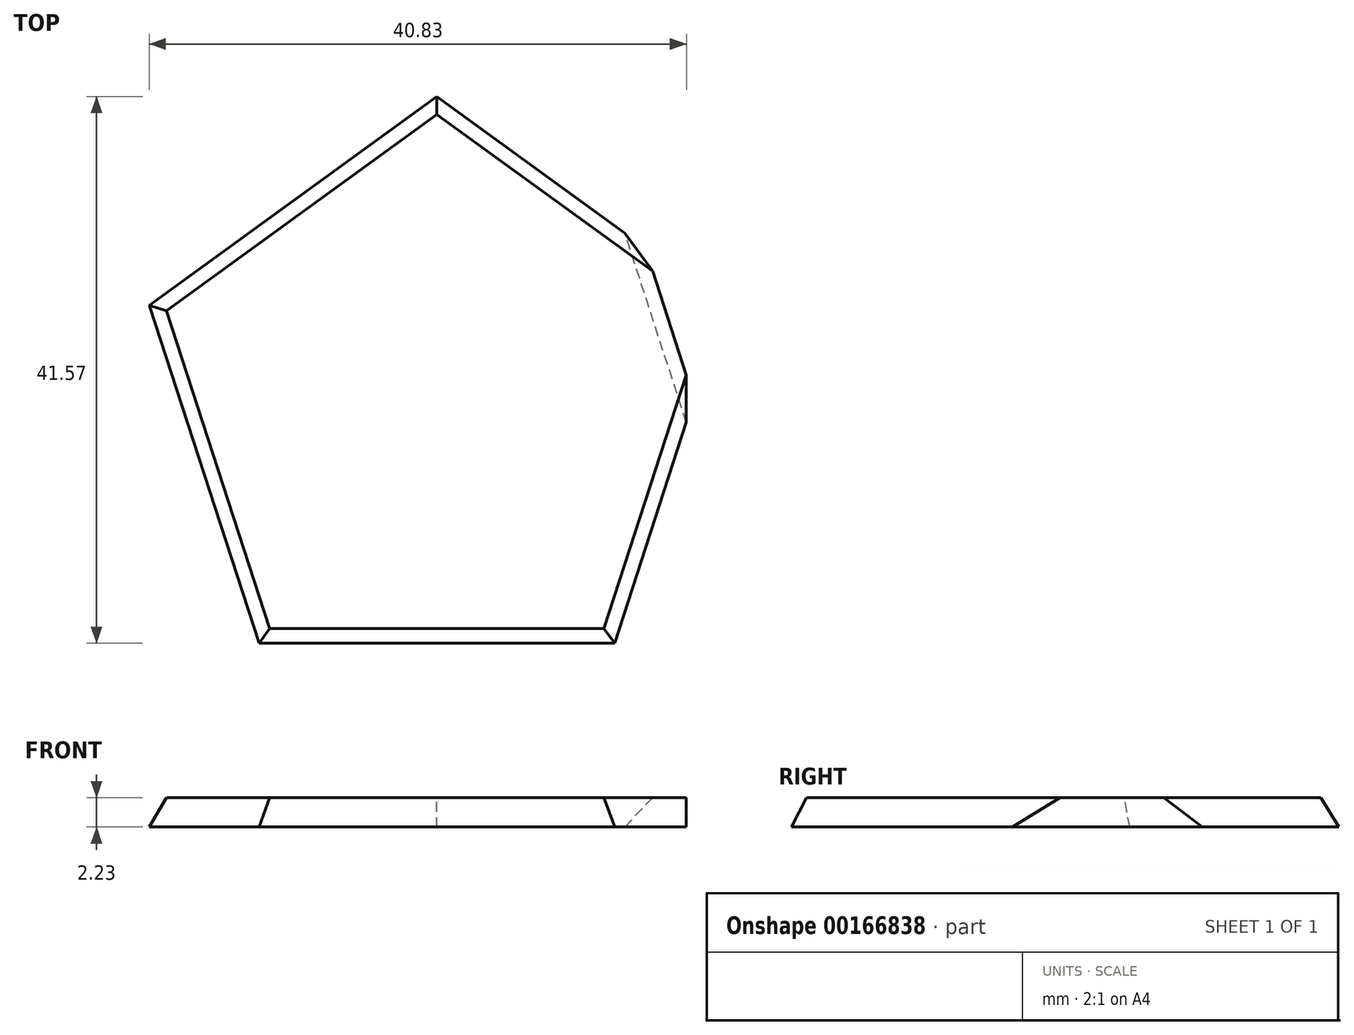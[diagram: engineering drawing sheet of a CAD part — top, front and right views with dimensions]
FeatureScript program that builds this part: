
annotation { "Feature Type Name" : "Feature", "Feature Type Description" : "" }
export const myFeature = defineFeature(function(context is Context, id is Id, definition is map)
    precondition{}
    {
        {
            var Q0;
            Q0=qCreatedBy(makeId("Top.planeOp"),FACE);
            var sketch = newSketch(context, id + "F0", { "sketchPlane" : qUnion([Q0])});
            skCircle(sketch, "E0.cCircle", {"center": v(0, 0) * mm, "radius": 17.48 * mm, "construction": true});
            skLineSegment(sketch, "E0.0", {"start": v(0, 21.6) * mm, "end": v(20.55, 6.68) * mm});
            skLineSegment(sketch, "E0.1", {"start": v(20.55, 6.68) * mm, "end": v(12.7, -17.48) * mm});
            skLineSegment(sketch, "E0.2", {"start": v(12.7, -17.48) * mm, "end": v(-12.7, -17.48) * mm});
            skLineSegment(sketch, "E0.3", {"start": v(-12.7, -17.48) * mm, "end": v(-20.55, 6.68) * mm});
            skLineSegment(sketch, "E0.4", {"start": v(-20.55, 6.68) * mm, "end": v(0, 21.6) * mm});
            skPoint(sketch, "E0.0.midPoint", {"position": v(10.27, 14.14) * mm});
            skSolve(sketch);
        }
        {
            var Q0;
            Q0=makeQuery(id+"F0.imprint","IMPRINT",FACE,{"disambiguationData":[TD([[makeQuery(id+"F0.imprint","IMPRINT",EDGE,{"derivedFrom":sQuery(id+"F0.wireOp",EDGE,"E0.0")}),-1.0]])]});
            extrude(context, id + "F1", {"entities" : qUnion([Q0]), "oppositeDirection" : true, "depth" : ((1 / sin(36 * degree)) * (sin(18 * degree) + 1)) * mm, "hasDraft" : true, "draftAngle" : acos(-1 / sqrt(5)) - 90 * degree, "hasSecondDirectionDraft" : true, "secondDirectionDraftAngle" : 90 * degree - (acos(-1 / 3) / 2), "secondDirectionDraftPullDirection" : true});
        }
        {
            var Q0;
            Q0=makeQuery(id+"F1.opExtrude","CAP_FACE",FACE,{"disambiguationData":[OSD([sQuery(id+"F0.wireOp",EDGE,"E0.0"),sQuery(id+"F0.wireOp",EDGE,"E0.1"),sQuery(id+"F0.wireOp",EDGE,"E0.2"),sQuery(id+"F0.wireOp",EDGE,"E0.3"),sQuery(id+"F0.wireOp",EDGE,"E0.4")])],"isStart":false});
            var sketch = newSketch(context, id + "F2", { "sketchPlane" : qUnion([Q0])});
            skCircle(sketch, "E1.cCircle", {"center": v(0, 0) * mm, "radius": 17.48 * mm, "construction": true});
            skLineSegment(sketch, "E1.0", {"start": v(20.55, 6.68) * mm, "end": v(12.7, -17.48) * mm});
            skLineSegment(sketch, "E1.1", {"start": v(12.7, -17.48) * mm, "end": v(-12.7, -17.48) * mm});
            skLineSegment(sketch, "E1.2", {"start": v(-12.7, -17.48) * mm, "end": v(-20.55, 6.68) * mm});
            skLineSegment(sketch, "E1.3", {"start": v(-20.55, 6.68) * mm, "end": v(0, 21.6) * mm});
            skLineSegment(sketch, "E1.4", {"start": v(0, 21.6) * mm, "end": v(20.55, 6.68) * mm});
            skPoint(sketch, "E1.0.midPoint", {"position": v(16.62, -5.4) * mm});
            skSolve(sketch);
        }
        {
            var Q0;
            Q0=makeQuery(id+"F2.imprint","IMPRINT",FACE,{"disambiguationData":[TD([[makeQuery(id+"F2.imprint","IMPRINT",EDGE,{"derivedFrom":sQuery(id+"F2.wireOp",EDGE,"E1.0")}),1.0]])]});
            extrude(context, id + "F3", {"entities" : qUnion([Q0]), "operationType" : NewBodyOperationType.REMOVE, "endBound" : BoundingType.THROUGH_ALL, "oppositeDirection" : true, "depth" : 56.64 * mm, "hasDraft" : true, "draftAngle" : acos(-1 / sqrt(5)) - 90 * degree, "draftPullDirection" : true});
        }
    });
